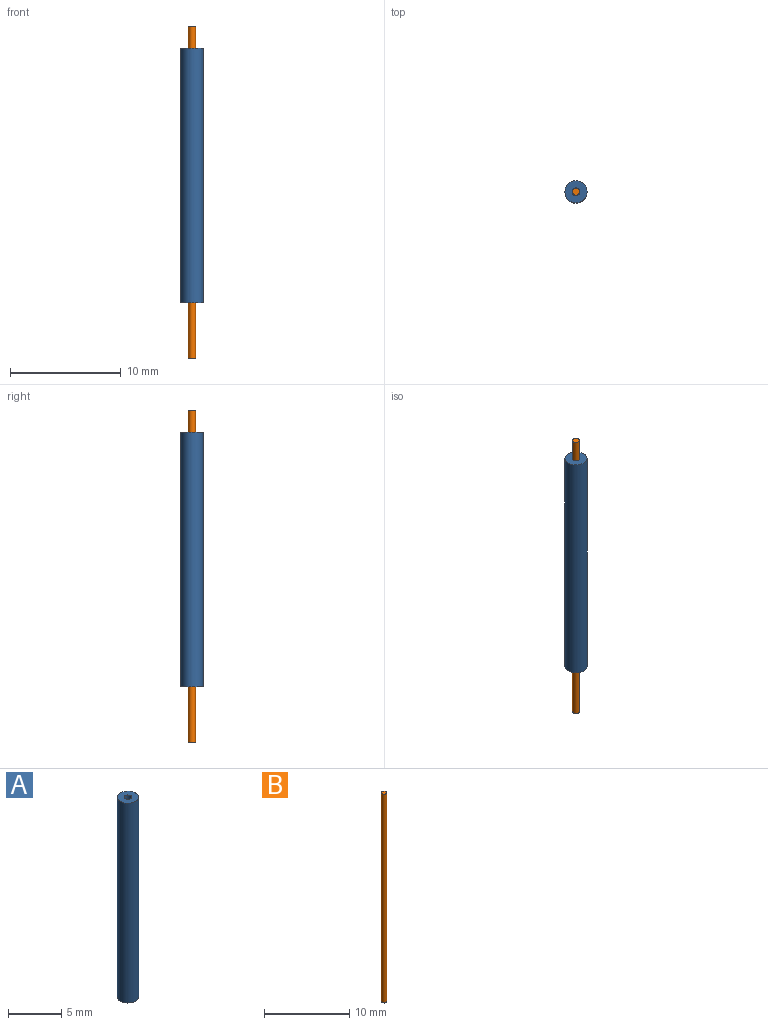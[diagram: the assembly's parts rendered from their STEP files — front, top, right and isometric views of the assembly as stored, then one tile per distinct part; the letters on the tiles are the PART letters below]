
ASSEMBLY  parts=2 mates=2
PART A: 4 faces, bbox 2x2x23 mm
  f0: cylinder r=0.35mm len=23mm, axis (0,0,-1), area 50.6mm2, adj f1,f3
  f1: plane 2x2mm, normal (0,0,1), area 2.8mm2, adj f0,f2
  f2: cylinder r=1mm len=23mm, axis (0,0,-1), area 144.5mm2, adj f1,f3
  f3: plane 2x2mm, normal (0,0,-1), area 2.8mm2, adj f0,f2
PART B: 3 faces, bbox 0.6x0.6x30 mm
  f0: plane 0.64x0.64mm, normal (0,0,-1), area 0.3mm2, adj f2
  f1: plane 0.64x0.64mm, normal (0,0,1), area 0.3mm2, adj f2
  f2: cylinder r=0.32mm len=30mm, axis (0,0,1), area 60.3mm2, adj f0,f1
PLACE A t=(-0.1,-0.02,-42.94)mm
PLACE B rot(axis=(0,0,1),90deg) t=(-0.1,-0.02,-42.94)mm
MATE planar B.f2 <-> A.f0  axis (0,0,1) through (-0.1,-0.02,-12.94)mm
MATE cylindrical A.f0 <-> B.f2  axis (0,0,-1) through (-0.1,-0.02,-14.94)mm
